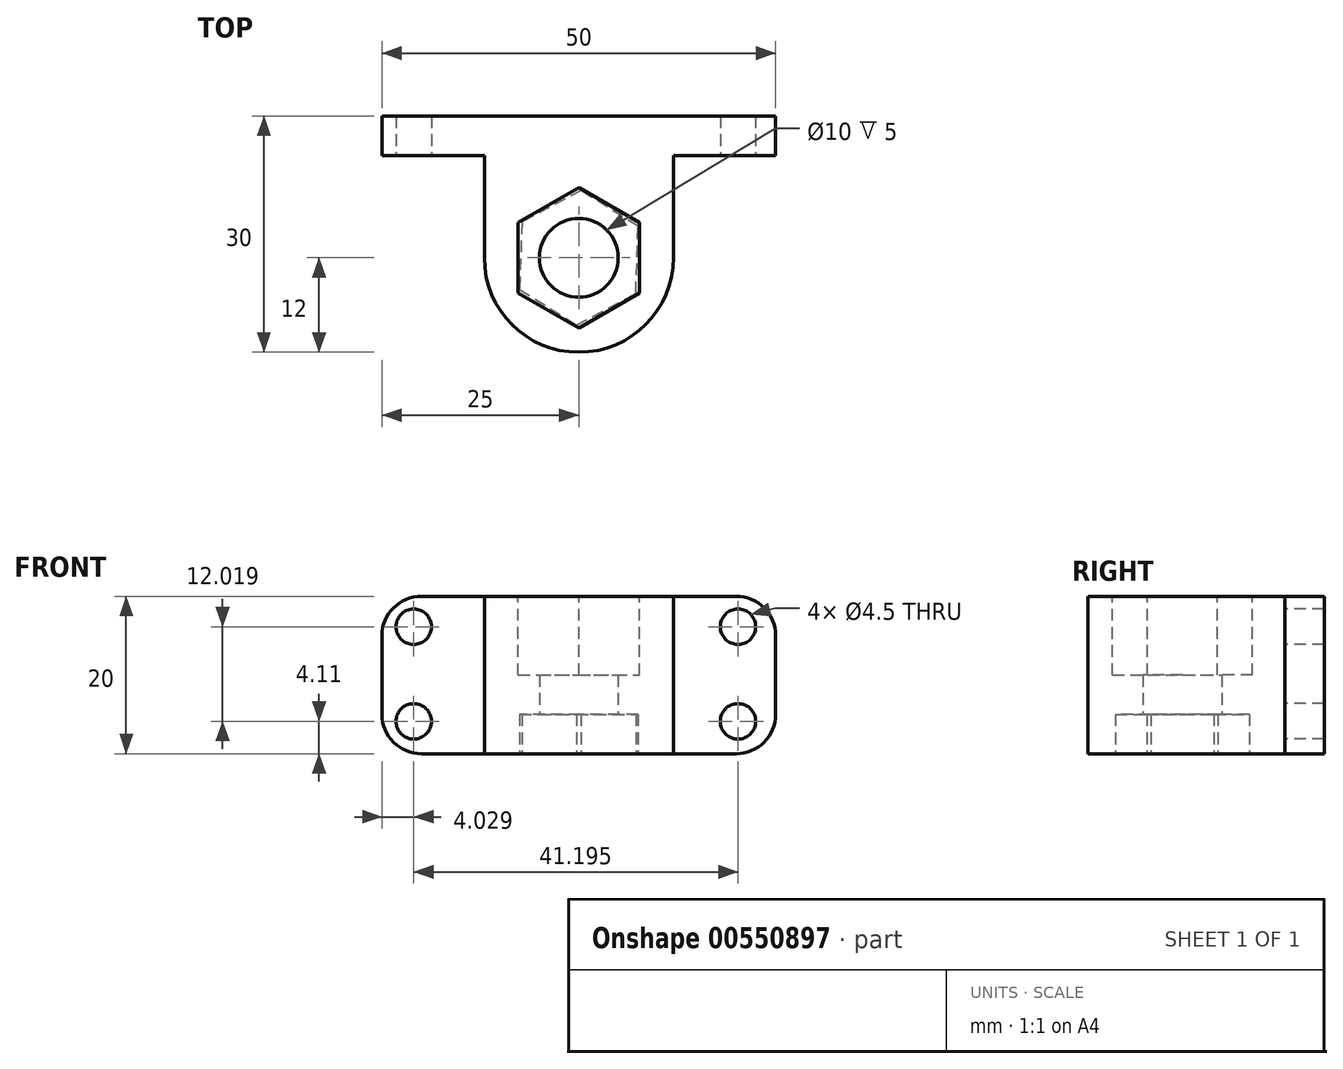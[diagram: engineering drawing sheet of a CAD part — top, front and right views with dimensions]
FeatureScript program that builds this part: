
annotation { "Feature Type Name" : "Feature", "Feature Type Description" : "" }
export const myFeature = defineFeature(function(context is Context, id is Id, definition is map)
    precondition{}
    {
        {
            var Q0;
            Q0=qCreatedBy(makeId("Top.planeOp"),FACE);
            var sketch = newSketch(context, id + "F0", { "sketchPlane" : qUnion([Q0])});
            skCircle(sketch, "E0", {"center": v(0, 0) * mm, "radius": 5 * mm});
            skLineSegment(sketch, "E1", {"start": v(-12, 18) * mm, "end": v(12, 18) * mm});
            skLineSegment(sketch, "E2", {"start": v(12, 18) * mm, "end": v(12, 0) * mm});
            skLineSegment(sketch, "E3", {"start": v(-12, 0) * mm, "end": v(-12, 18) * mm});
            skArc(sketch, "E4", {"start": v(-12, 0) * mm, "mid": v(0, -12) * mm, "end": v(12, 0) * mm});
            skSolve(sketch);
        }
        {
            var Q0;
            Q0 = qSketchRegion(id + "F0", true);
            extrude(context, id + "F1", {"entities" : qUnion([Q0]), "depth" : 20 * mm, "offsetDistance" : 25 * mm});
        }
        {
            var Q0;
            Q0=makeQuery(id+"F1.opExtrude","CAP_FACE",FACE,{"disambiguationData":[OSD([sQuery(id+"F0.wireOp",EDGE,"E0"),sQuery(id+"F0.wireOp",EDGE,"E1"),sQuery(id+"F0.wireOp",EDGE,"E2"),sQuery(id+"F0.wireOp",EDGE,"E3"),sQuery(id+"F0.wireOp",EDGE,"E4")])],"isStart":false});
            var sketch = newSketch(context, id + "F2", { "sketchPlane" : qUnion([Q0])});
            skLineSegment(sketch, "E5.bottom", {"start": v(-25, 18) * mm, "end": v(25, 18) * mm});
            skLineSegment(sketch, "E5.top", {"start": v(-25, 13) * mm, "end": v(25, 13) * mm});
            skLineSegment(sketch, "E5.left", {"start": v(-25, 18) * mm, "end": v(-25, 13) * mm});
            skLineSegment(sketch, "E5.right", {"start": v(25, 18) * mm, "end": v(25, 13) * mm});
            skLineSegment(sketch, "E6", {"start": v(0, 18) * mm, "end": v(0, 0) * mm, "construction": true});
            skSolve(sketch);
        }
        {
            var Q0;
            Q0 = qSketchRegion(id + "F2", true);
            var Q1;
            Q1=makeQuery(id+"F1.opExtrude","CAP_FACE",FACE,{"disambiguationData":[OSD([sQuery(id+"F0.wireOp",EDGE,"E0"),sQuery(id+"F0.wireOp",EDGE,"E1"),sQuery(id+"F0.wireOp",EDGE,"E2"),sQuery(id+"F0.wireOp",EDGE,"E3"),sQuery(id+"F0.wireOp",EDGE,"E4")])],"isStart":true});
            extrude(context, id + "F3", {"entities" : qUnion([Q0]), "operationType" : NewBodyOperationType.ADD, "endBound" : BoundingType.UP_TO_SURFACE, "oppositeDirection" : true, "depth" : 30 * mm, "endBoundEntityFace" : qUnion([Q1]), "offsetDistance" : 25 * mm});
        }
        {
            var Q0;
            Q0=makeQuery(id+"F3.opExtrude","SWEPT_FACE",FACE,{"disambiguationData":[OSD([sQuery(id+"F2.wireOp",EDGE,"E5.top")])]});
            var sketch = newSketch(context, id + "F4", { "sketchPlane" : qUnion([Q0])});
            skCircle(sketch, "E7", {"center": v(-20.97, 16.13) * mm, "radius": 2.25 * mm});
            skCircle(sketch, "E8", {"center": v(20.22, 16.13) * mm, "radius": 2.25 * mm});
            skCircle(sketch, "E9", {"center": v(-20.97, 4.11) * mm, "radius": 2.25 * mm});
            skCircle(sketch, "E10", {"center": v(20.22, 4.11) * mm, "radius": 2.25 * mm});
            skSolve(sketch);
        }
        {
            var Q0;
            Q0 = qSketchRegion(id + "F4", true);
            extrude(context, id + "F5", {"entities" : qUnion([Q0]), "operationType" : NewBodyOperationType.REMOVE, "oppositeDirection" : true, "depth" : 25 * mm, "offsetDistance" : 25 * mm});
        }
        {
            var Q0;
            Q0=makeQuery(id+"F3.opExtrude","CAP_EDGE",EDGE,{"disambiguationData":[OSD([sQuery(id+"F2.wireOp",EDGE,"E5.right")])],"isStart":false});
            var Q1;
            Q1=makeQuery(id+"F3.opExtrude","CAP_EDGE",EDGE,{"disambiguationData":[OSD([sQuery(id+"F2.wireOp",EDGE,"E5.left")])],"isStart":false});
            var Q2;
            Q2=makeQuery(id+"F3.opExtrude","CAP_EDGE",EDGE,{"disambiguationData":[OSD([sQuery(id+"F2.wireOp",EDGE,"E5.left")])],"isStart":true});
            var Q3;
            Q3=makeQuery(id+"F3.opExtrude","CAP_EDGE",EDGE,{"disambiguationData":[OSD([sQuery(id+"F2.wireOp",EDGE,"E5.right")])],"isStart":true});
            fillet(context, id + "F6", {"entities" : qUnion([Q0, Q1, Q2, Q3]), "radius" : 5 * mm, "tangentPropagation" : true, "allowEdgeOverflow" : false});
        }
        {
            var Q0;
            Q0=makeQuery(id+"F1.opExtrude","CAP_FACE",FACE,{"disambiguationData":[OSD([sQuery(id+"F0.wireOp",EDGE,"E0"),sQuery(id+"F0.wireOp",EDGE,"E1"),sQuery(id+"F0.wireOp",EDGE,"E2"),sQuery(id+"F0.wireOp",EDGE,"E3"),sQuery(id+"F0.wireOp",EDGE,"E4")])],"isStart":false});
            var sketch = newSketch(context, id + "F7", { "sketchPlane" : qUnion([Q0])});
            skCircle(sketch, "E11.cCircle", {"center": v(0, 0) * mm, "radius": 7.7 * mm, "construction": true});
            skLineSegment(sketch, "E11.0", {"start": v(0, 8.9) * mm, "end": v(7.7, 4.45) * mm});
            skLineSegment(sketch, "E11.1", {"start": v(7.7, 4.45) * mm, "end": v(7.7, -4.45) * mm});
            skLineSegment(sketch, "E11.2", {"start": v(7.7, -4.45) * mm, "end": v(0, -8.9) * mm});
            skLineSegment(sketch, "E11.3", {"start": v(0, -8.9) * mm, "end": v(-7.7, -4.45) * mm});
            skLineSegment(sketch, "E11.4", {"start": v(-7.7, -4.45) * mm, "end": v(-7.7, 4.45) * mm});
            skLineSegment(sketch, "E11.5", {"start": v(-7.7, 4.45) * mm, "end": v(0, 8.9) * mm});
            skPoint(sketch, "E11.0.midPoint", {"position": v(3.85, 6.67) * mm});
            skSolve(sketch);
        }
        {
            var Q0;
            Q0 = qSketchRegion(id + "F7", true);
            extrude(context, id + "F8", {"entities" : qUnion([Q0]), "operationType" : NewBodyOperationType.REMOVE, "oppositeDirection" : true, "depth" : 10 * mm, "offsetDistance" : 25 * mm});
        }
        {
            var Q0;
            Q0=makeQuery(id+"F1.opExtrude","CAP_FACE",FACE,{"disambiguationData":[OSD([sQuery(id+"F0.wireOp",EDGE,"E0"),sQuery(id+"F0.wireOp",EDGE,"E1"),sQuery(id+"F0.wireOp",EDGE,"E2"),sQuery(id+"F0.wireOp",EDGE,"E3"),sQuery(id+"F0.wireOp",EDGE,"E4")])],"isStart":true});
            var sketch = newSketch(context, id + "F9", { "sketchPlane" : qUnion([Q0])});
            skCircle(sketch, "E12.cCircle", {"center": v(0, 0) * mm, "radius": 7.39 * mm, "construction": true});
            skLineSegment(sketch, "E12.0", {"start": v(-7.53, 4.01) * mm, "end": v(-0.3, 8.53) * mm});
            skLineSegment(sketch, "E12.1", {"start": v(-0.3, 8.53) * mm, "end": v(7.24, 4.52) * mm});
            skLineSegment(sketch, "E12.2", {"start": v(7.24, 4.52) * mm, "end": v(7.53, -4.01) * mm});
            skLineSegment(sketch, "E12.3", {"start": v(7.53, -4.01) * mm, "end": v(0.3, -8.53) * mm});
            skLineSegment(sketch, "E12.4", {"start": v(0.3, -8.53) * mm, "end": v(-7.24, -4.52) * mm});
            skLineSegment(sketch, "E12.5", {"start": v(-7.24, -4.52) * mm, "end": v(-7.53, 4.01) * mm});
            skPoint(sketch, "E12.0.midPoint", {"position": v(-3.91, 6.27) * mm});
            skSolve(sketch);
        }
        {
            var Q0;
            Q0 = qSketchRegion(id + "F9", true);
            extrude(context, id + "F10", {"entities" : qUnion([Q0]), "operationType" : NewBodyOperationType.REMOVE, "oppositeDirection" : true, "depth" : 5 * mm, "offsetDistance" : 25 * mm});
        }
    });
